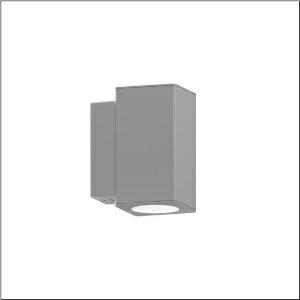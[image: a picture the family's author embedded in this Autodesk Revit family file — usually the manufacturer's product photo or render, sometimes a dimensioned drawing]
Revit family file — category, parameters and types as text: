
# Revit family: cl_31_wand_5cl563623
name_source: partatom
category: Lighting Fixtures
units: mm (PartAtom-declared; Revit-internal decimal feet)

## family parameters
Cut with Voids When Loaded = No
Host = Face
Light Source = No
Part Type = Normal
Room Calculation Point = No
Round Connector Dimension = Use Diameter
Shared = No

## types (1)
- --- (1 x LED, 600 lm, 5.4 W, 3000K)
    Apparent Load = 5 VA
    CIE Flux Codes = 98 100 100 50 100
    Color Rendering = 80
    Color Temperature = 3000K
    Default Elevation = 1800 mm
    Description = CL 31 Wall, wall luminaire, primary light control with reflector, of aluminium, primary optical cover: cover panel, of glass, transparent, light emission: up/down distribution, primary light characteristic: symmetric, installation type: surface-mounted, for 2x LED, rated luminous flux: 300lm, luminous efficacy: 110lm/W, light colour: 830, colour temperature: 3000K, control gear: ECG DALI, with terminal, 5-pole, max. 2.5mm², mains connection: 220..240V, AC, 50/60Hz, rated input power: 5.5W, luminaire housing, square, of aluminium, powder-coated, Siteco® metallic grey, length: 143mm, width: 100mm, height: 186mm, protection rating (complete): IP65, insulation class (complete): insulation class I (protective earthing), certification: CE, ENEC, impact resistance: IK08, permissible operating ambient temperature for outdoor applications: -20..+50°C, packaging unit: 1 piece
    Height = 186 mm
    Lamp = 1 x LED
    Lamp Light Flux = 600 lm
    Lamp Power = 5.4 W
    Lamp count = 1
    Length = 100 mm  [stored 0.328084 ft]
    Luminous efficacy = 111 lm/W
    Manufacturer = Siteco
    ModVariant = No
    Model = 5CL563623
    Mounting Place = Wall
    Mounting Type = Surface mounted
    Number of Poles = 1
    OnlyDefault = Yes
    Power Factor = 1
    Product Name = CL 31 Wand
    Product group = wall luminaire
    ProductGroupID = 2002
    Protection Class = Protection class I
    Protection Degree = IP 65
    RLX_Detail_Level = 1
    RLX_Emergency_Light_Flux = 0 lm
    RLX_Emergency_Type = 0
    RLX_Emergency_Type_DB = No
    RlxData = <blob elided: 40349 chars, md5=0b574106>
    Socket = socket
    Standby Power = 0 W
    System Light Flux = 600 lm
    System Power = 5 W
    Type Comments = factory setting: luminous flux: 100 % | dim-lin: 254 | 135 mA
    Type Image = l_1006895.jpg
    URL = http://relux.com
    VarID = @adj_130517
    Voltage = 0 V
    Weight = 0.00 kg
    Width = 143 mm

note: [stored X ft] marks values corroborated as IEEE doubles in the binary element streams (Revit-internal decimal feet)

## geometry (parser evidence)
native form markers: Blend x4, Sweep x13
no freeform markers — native parametric forms only
